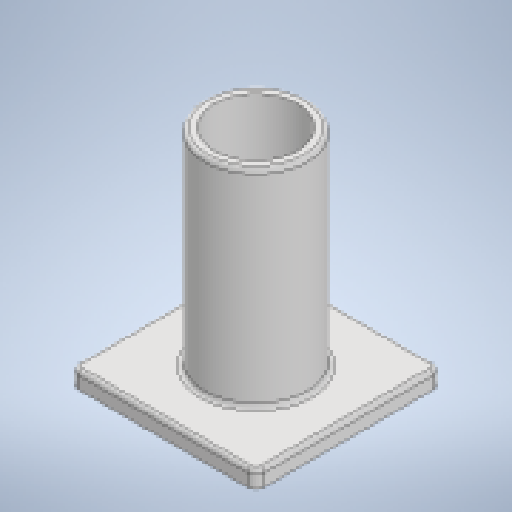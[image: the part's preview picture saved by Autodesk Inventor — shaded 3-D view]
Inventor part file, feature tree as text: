
AUTODESK INVENTOR PART (.ipt)
format: ipt  version: 2025 (Build 290162000, 162)  size: 567,808 bytes
history: native  units: mm
features: extrude x2, fillet x2, other x1, sketch x1
ambient origin geometry x8: Origin, YZ Plane, XZ Plane, XY Plane, X Axis, Y Axis, Z Axis, Center Point
bodies: Body1 (feature_tree)
feature tree (6):
  other  "ソリッド1"
  extrude  "底"  Depth=45.0mm
  extrude  "棒"  Depth=45.0mm
  fillet  "フィレット1"  Radius=2.0mm
  fillet  "フィレット2"  Radius=4.0mm
  sketch  "スケッチ2"
